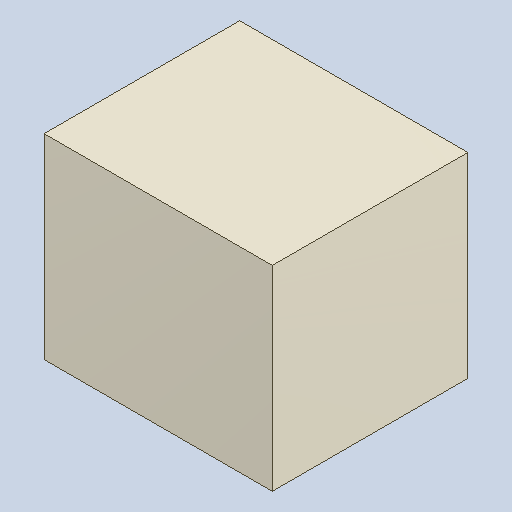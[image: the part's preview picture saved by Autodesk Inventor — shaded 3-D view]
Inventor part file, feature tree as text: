
AUTODESK INVENTOR PART (.ipt)
format: ipt  version: 2023.4 (Build 274418000, 418)  size: 82,432 bytes
history: native  units: mm
features: extrude x1
ambient origin geometry x8: Origin, YZ Plane, XZ Plane, XY Plane, X Axis, Y Axis, Z Axis, Center Point
bodies: Solid1 (feature_tree)
feature tree (1):
  extrude  "Extruded_14"  [1 undecoded]
note: 1 required parameter value undecoded (feature->parameter linkage not recoverable at this tier; creation-order binding heuristic only, values carry confidence <= 0.55)
